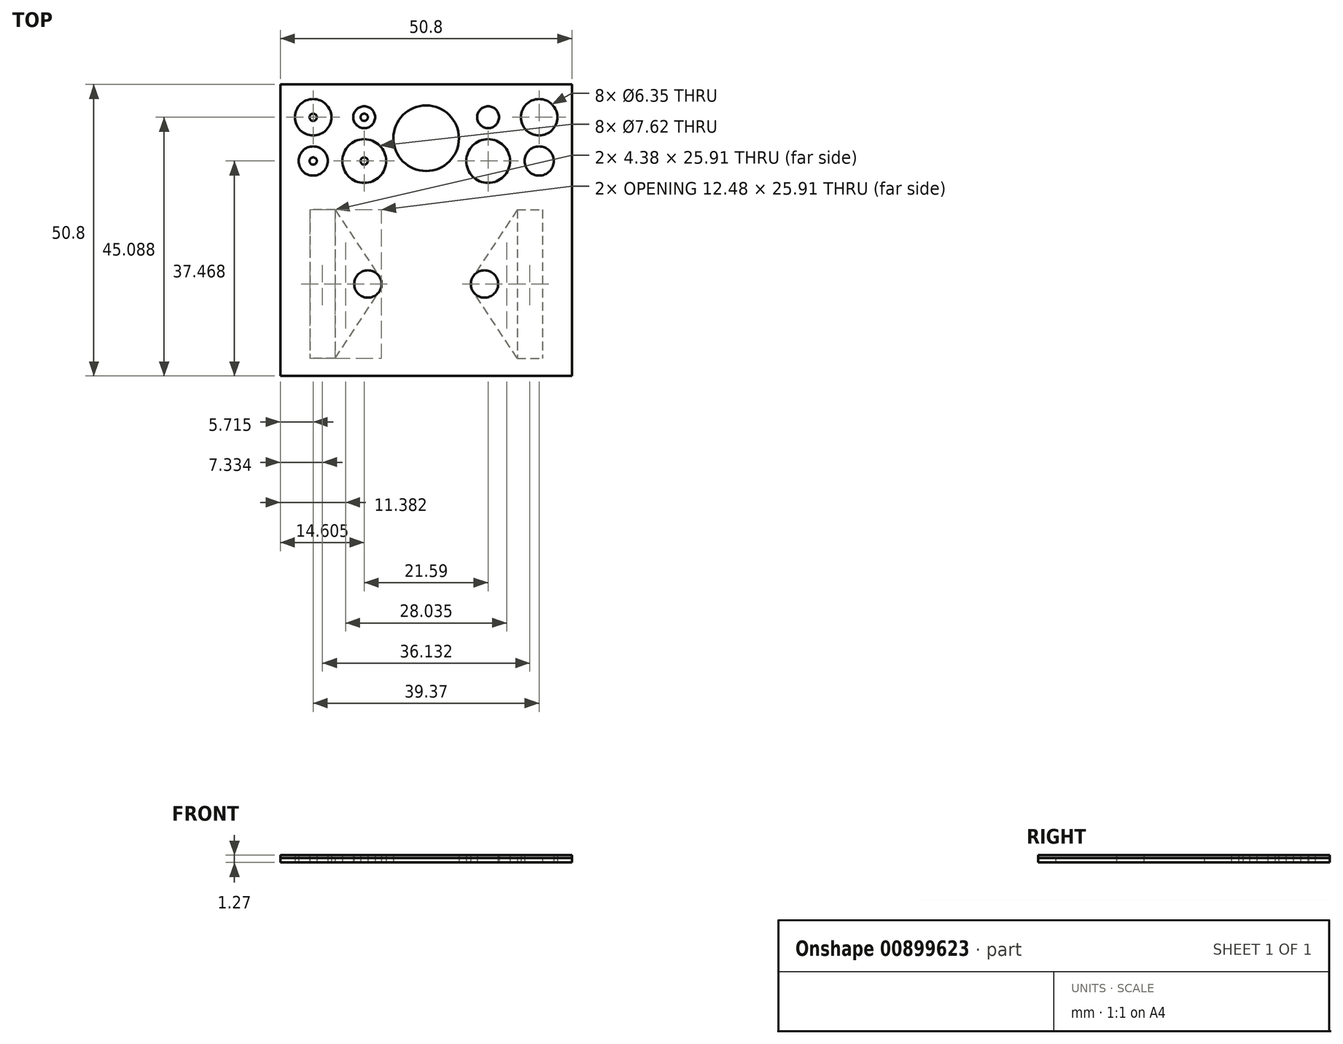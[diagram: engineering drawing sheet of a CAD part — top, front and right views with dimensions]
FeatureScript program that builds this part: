
annotation { "Feature Type Name" : "Feature", "Feature Type Description" : "" }
export const myFeature = defineFeature(function(context is Context, id is Id, definition is map)
    precondition{}
    {
        {
            var Q0;
            Q0=qCreatedBy(makeId("Top.planeOp"),FACE);
            var sketch = newSketch(context, id + "F0", { "sketchPlane" : qUnion([Q0])});
            skLineSegment(sketch, "E0.bottom", {"start": v(25.4, 34.77) * mm, "end": v(-25.4, 34.77) * mm});
            skLineSegment(sketch, "E0.top", {"start": v(25.4, -16.03) * mm, "end": v(-25.4, -16.03) * mm});
            skLineSegment(sketch, "E0.left", {"start": v(25.4, 34.77) * mm, "end": v(25.4, -16.03) * mm});
            skLineSegment(sketch, "E0.right", {"start": v(-25.4, 34.77) * mm, "end": v(-25.4, -16.03) * mm});
            skLineSegment(sketch, "E1", {"start": v(15.88, 12.95) * mm, "end": v(8.17, 1.31) * mm});
            skLineSegment(sketch, "E2", {"start": v(15.88, -12.95) * mm, "end": v(8.17, -1.31) * mm});
            skLineSegment(sketch, "E3.bottom", {"start": v(15.88, 12.95) * mm, "end": v(20.26, 12.95) * mm});
            skLineSegment(sketch, "E3.top", {"start": v(15.88, -12.95) * mm, "end": v(20.26, -12.95) * mm});
            skLineSegment(sketch, "E3.right", {"start": v(20.26, 12.95) * mm, "end": v(20.26, -12.95) * mm});
            skLineSegment(sketch, "E4.MirrorCS", {"start": v(-20.26, 12.95) * mm, "end": v(-20.26, -12.95) * mm});
            skLineSegment(sketch, "E5.MirrorCS", {"start": v(-15.88, 12.95) * mm, "end": v(-20.26, 12.95) * mm});
            skLineSegment(sketch, "E6.MirrorCS", {"start": v(-15.88, 12.95) * mm, "end": v(-8.17, 1.31) * mm});
            skLineSegment(sketch, "E7.MirrorCS", {"start": v(-15.88, -12.95) * mm, "end": v(-8.17, -1.31) * mm});
            skLineSegment(sketch, "E8.MirrorCS", {"start": v(-15.88, -12.95) * mm, "end": v(-20.26, -12.95) * mm});
            skLineSegment(sketch, "E9", {"start": v(0, -16.03) * mm, "end": v(0, 0) * mm, "construction": true});
            skLineSegment(sketch, "E10", {"start": v(0, 0) * mm, "end": v(20.26, 0) * mm, "construction": true});
            skLineSegment(sketch, "E11", {"start": v(-25.4, 16.03) * mm, "end": v(25.4, 16.03) * mm, "construction": true});
            skLineSegment(sketch, "E12", {"start": v(0, 16.03) * mm, "end": v(0, 34.77) * mm, "construction": true});
            skLineSegment(sketch, "E13", {"start": v(10.8, 21.44) * mm, "end": v(19.69, 21.44) * mm, "construction": true});
            skLineSegment(sketch, "E14", {"start": v(19.69, 21.44) * mm, "end": v(19.69, 29.06) * mm, "construction": true});
            skLineSegment(sketch, "E15", {"start": v(19.69, 29.06) * mm, "end": v(10.8, 29.06) * mm, "construction": true});
            skLineSegment(sketch, "E16", {"start": v(10.8, 29.06) * mm, "end": v(10.8, 21.44) * mm, "construction": true});
            skCircle(sketch, "E17", {"center": v(0, 25.4) * mm, "radius": 5.72 * mm});
            skCircle(sketch, "E18", {"center": v(10.8, 29.06) * mm, "radius": 1.9 * mm});
            skCircle(sketch, "E19", {"center": v(10.8, 21.44) * mm, "radius": 3.81 * mm});
            skCircle(sketch, "E20", {"center": v(19.69, 29.06) * mm, "radius": 3.18 * mm});
            skCircle(sketch, "E21", {"center": v(19.69, 21.44) * mm, "radius": 2.54 * mm});
            skCircle(sketch, "E22.MirrorC", {"center": v(-10.8, 29.06) * mm, "radius": 1.9 * mm});
            skCircle(sketch, "E23.MirrorC", {"center": v(-10.8, 21.44) * mm, "radius": 3.81 * mm});
            skCircle(sketch, "E24.MirrorC", {"center": v(-19.69, 29.06) * mm, "radius": 3.18 * mm});
            skCircle(sketch, "E25.MirrorC", {"center": v(-19.69, 21.44) * mm, "radius": 2.54 * mm});
            skLineSegment(sketch, "E26", {"start": v(-15.88, 12.95) * mm, "end": v(-15.88, -12.95) * mm});
            skLineSegment(sketch, "E27", {"start": v(15.88, 12.95) * mm, "end": v(15.88, -12.95) * mm});
            skCircle(sketch, "E28", {"center": v(-10.16, 0) * mm, "radius": 2.38 * mm});
            skCircle(sketch, "E29", {"center": v(10.16, 0) * mm, "radius": 2.38 * mm});
            skCircle(sketch, "E30", {"center": v(-19.69, 29.06) * mm, "radius": 0.64 * mm});
            skCircle(sketch, "E31", {"center": v(-10.8, 29.06) * mm, "radius": 0.64 * mm});
            skCircle(sketch, "E32", {"center": v(-10.8, 21.44) * mm, "radius": 0.64 * mm});
            skCircle(sketch, "E33", {"center": v(-19.69, 21.44) * mm, "radius": 0.64 * mm});
            skSolve(sketch);
        }
        {
            var Q0;
            Q0 = qSketchRegion(id + "F0", true);
            extrude(context, id + "F1", {"entities" : qUnion([Q0]), "depth" : 0.76 * mm, "offsetDistance" : 25.4 * mm});
        }
        {
            var Q0;
            Q0 = qSketchRegion(id + "F0", true);
            var Q1;
            Q1=makeQuery(id+"F0.imprint","IMPRINT",FACE,{"disambiguationData":[TD([[makeQuery(id+"F0.imprint","IMPRINT",EDGE,{"derivedFrom":sQuery(id+"F0.wireOp",EDGE,"E4.MirrorCS")}),1.0]])]});
            var Q2;
            {var subQ0=sQuery(id+"F0.wireOp",EDGE,"E6.MirrorCS");Q2=makeQuery(id+"F0.imprint","IMPRINT",FACE,{"disambiguationData":[TD([[makeQuery(id+"F0.imprint","IMPRINT",EDGE,{"derivedFrom":subQ0}),-1.0]])]});}
            var Q3;
            {var subQ0=sQuery(id+"F0.wireOp",EDGE,"E28");var subQ1=makeQuery(id+"F0.imprint","INTERSECT",VERTEX,{"derivedFrom":[sQuery(id+"F0.wireOp",EDGE,"E6.MirrorCS"),subQ0]});Q3=makeQuery(id+"F0.imprint","IMPRINT",FACE,{"disambiguationData":[TD([[makeQuery(id+"F0.imprint","IMPRINT",EDGE,{"disambiguationData":[TD([[subQ1,-1.0]])],"derivedFrom":subQ0}),1.0]])]});}
            var Q4;
            Q4=makeQuery(id+"F0.imprint","IMPRINT",FACE,{"disambiguationData":[TD([[makeQuery(id+"F0.imprint","IMPRINT",EDGE,{"derivedFrom":sQuery(id+"F0.wireOp",EDGE,"E3.bottom")}),-1.0]])]});
            var Q5;
            {var subQ0=sQuery(id+"F0.wireOp",EDGE,"E1");Q5=makeQuery(id+"F0.imprint","IMPRINT",FACE,{"disambiguationData":[TD([[makeQuery(id+"F0.imprint","IMPRINT",EDGE,{"derivedFrom":subQ0}),1.0]])]});}
            var Q6;
            {var subQ0=sQuery(id+"F0.wireOp",EDGE,"E29");var subQ1=makeQuery(id+"F0.imprint","INTERSECT",VERTEX,{"derivedFrom":[sQuery(id+"F0.wireOp",EDGE,"E1"),subQ0]});Q6=makeQuery(id+"F0.imprint","IMPRINT",FACE,{"disambiguationData":[TD([[makeQuery(id+"F0.imprint","IMPRINT",EDGE,{"disambiguationData":[TD([[subQ1,-1.0]])],"derivedFrom":subQ0}),1.0]])]});}
            var Q7;
            Q7=makeQuery(id+"F0.imprint","IMPRINT",FACE,{"disambiguationData":[TD([[makeQuery(id+"F0.imprint","IMPRINT",EDGE,{"derivedFrom":sQuery(id+"F0.wireOp",EDGE,"E25.MirrorC")}),-1.0]])]});
            var Q8;
            Q8=makeQuery(id+"F0.imprint","IMPRINT",FACE,{"disambiguationData":[TD([[makeQuery(id+"F0.imprint","IMPRINT",EDGE,{"derivedFrom":sQuery(id+"F0.wireOp",EDGE,"E24.MirrorC")}),-1.0]])]});
            var Q9;
            Q9=makeQuery(id+"F0.imprint","IMPRINT",FACE,{"disambiguationData":[TD([[makeQuery(id+"F0.imprint","IMPRINT",EDGE,{"derivedFrom":sQuery(id+"F0.wireOp",EDGE,"E22.MirrorC")}),-1.0]])]});
            var Q10;
            Q10=makeQuery(id+"F0.imprint","IMPRINT",FACE,{"disambiguationData":[TD([[makeQuery(id+"F0.imprint","IMPRINT",EDGE,{"derivedFrom":sQuery(id+"F0.wireOp",EDGE,"E23.MirrorC")}),-1.0]])]});
            var Q11;
            Q11=makeQuery(id+"F0.imprint","IMPRINT",FACE,{"disambiguationData":[TD([[makeQuery(id+"F0.imprint","IMPRINT",EDGE,{"derivedFrom":sQuery(id+"F0.wireOp",EDGE,"E33")}),1.0]])]});
            var Q12;
            Q12=makeQuery(id+"F0.imprint","IMPRINT",FACE,{"disambiguationData":[TD([[makeQuery(id+"F0.imprint","IMPRINT",EDGE,{"derivedFrom":sQuery(id+"F0.wireOp",EDGE,"E32")}),1.0]])]});
            var Q13;
            Q13=makeQuery(id+"F0.imprint","IMPRINT",FACE,{"disambiguationData":[TD([[makeQuery(id+"F0.imprint","IMPRINT",EDGE,{"derivedFrom":sQuery(id+"F0.wireOp",EDGE,"E31")}),1.0]])]});
            var Q14;
            Q14=makeQuery(id+"F0.imprint","IMPRINT",FACE,{"disambiguationData":[TD([[makeQuery(id+"F0.imprint","IMPRINT",EDGE,{"derivedFrom":sQuery(id+"F0.wireOp",EDGE,"E30")}),1.0]])]});
            extrude(context, id + "F2", {"entities" : qUnion([Q0, Q1, Q2, Q3, Q4, Q5, Q6, Q7, Q8, Q9, Q10, Q11, Q12, Q13, Q14]), "depth" : 1.27 * mm, "offsetDistance" : 25.4 * mm});
        }
        {
            var Q0;
            Q0 = qSketchRegion(id + "F0", true);
            var Q1;
            {var subQ0=sQuery(id+"F0.wireOp",EDGE,"E28");var subQ1=makeQuery(id+"F0.imprint","INTERSECT",VERTEX,{"derivedFrom":[sQuery(id+"F0.wireOp",EDGE,"E6.MirrorCS"),subQ0]});Q1=makeQuery(id+"F0.imprint","IMPRINT",FACE,{"disambiguationData":[TD([[makeQuery(id+"F0.imprint","IMPRINT",EDGE,{"disambiguationData":[TD([[subQ1,-1.0]])],"derivedFrom":subQ0}),1.0]])]});}
            var Q2;
            {var subQ0=sQuery(id+"F0.wireOp",EDGE,"E6.MirrorCS");Q2=makeQuery(id+"F0.imprint","IMPRINT",FACE,{"disambiguationData":[TD([[makeQuery(id+"F0.imprint","IMPRINT",EDGE,{"derivedFrom":subQ0}),-1.0]])]});}
            var Q3;
            {var subQ0=sQuery(id+"F0.wireOp",EDGE,"E29");var subQ1=makeQuery(id+"F0.imprint","INTERSECT",VERTEX,{"derivedFrom":[sQuery(id+"F0.wireOp",EDGE,"E1"),subQ0]});Q3=makeQuery(id+"F0.imprint","IMPRINT",FACE,{"disambiguationData":[TD([[makeQuery(id+"F0.imprint","IMPRINT",EDGE,{"disambiguationData":[TD([[subQ1,-1.0]])],"derivedFrom":subQ0}),1.0]])]});}
            var Q4;
            {var subQ0=sQuery(id+"F0.wireOp",EDGE,"E1");Q4=makeQuery(id+"F0.imprint","IMPRINT",FACE,{"disambiguationData":[TD([[makeQuery(id+"F0.imprint","IMPRINT",EDGE,{"derivedFrom":subQ0}),1.0]])]});}
            extrude(context, id + "F3", {"entities" : qUnion([Q0, Q1, Q2, Q3, Q4]), "depth" : 0.76 * mm, "offsetDistance" : 25.4 * mm});
        }
        {
            var Q0;
            Q0 = qSketchRegion(id + "F0", true);
            var Q1;
            Q1=makeQuery(id+"F0.imprint","IMPRINT",FACE,{"disambiguationData":[TD([[makeQuery(id+"F0.imprint","IMPRINT",EDGE,{"derivedFrom":sQuery(id+"F0.wireOp",EDGE,"E4.MirrorCS")}),1.0]])]});
            var Q2;
            Q2=makeQuery(id+"F0.imprint","IMPRINT",FACE,{"disambiguationData":[TD([[makeQuery(id+"F0.imprint","IMPRINT",EDGE,{"derivedFrom":sQuery(id+"F0.wireOp",EDGE,"E3.bottom")}),-1.0]])]});
            var Q3;
            {var subQ0=sQuery(id+"F0.wireOp",EDGE,"E6.MirrorCS");Q3=makeQuery(id+"F0.imprint","IMPRINT",FACE,{"disambiguationData":[TD([[makeQuery(id+"F0.imprint","IMPRINT",EDGE,{"derivedFrom":subQ0}),-1.0]])]});}
            var Q4;
            {var subQ0=sQuery(id+"F0.wireOp",EDGE,"E1");Q4=makeQuery(id+"F0.imprint","IMPRINT",FACE,{"disambiguationData":[TD([[makeQuery(id+"F0.imprint","IMPRINT",EDGE,{"derivedFrom":subQ0}),1.0]])]});}
            var Q5;
            Q5=makeQuery(id+"F0.imprint","IMPRINT",FACE,{"disambiguationData":[TD([[makeQuery(id+"F0.imprint","IMPRINT",EDGE,{"derivedFrom":sQuery(id+"F0.wireOp",EDGE,"E25.MirrorC")}),-1.0]])]});
            var Q6;
            Q6=makeQuery(id+"F0.imprint","IMPRINT",FACE,{"disambiguationData":[TD([[makeQuery(id+"F0.imprint","IMPRINT",EDGE,{"derivedFrom":sQuery(id+"F0.wireOp",EDGE,"E24.MirrorC")}),-1.0]])]});
            var Q7;
            Q7=makeQuery(id+"F0.imprint","IMPRINT",FACE,{"disambiguationData":[TD([[makeQuery(id+"F0.imprint","IMPRINT",EDGE,{"derivedFrom":sQuery(id+"F0.wireOp",EDGE,"E23.MirrorC")}),-1.0]])]});
            var Q8;
            Q8=makeQuery(id+"F0.imprint","IMPRINT",FACE,{"disambiguationData":[TD([[makeQuery(id+"F0.imprint","IMPRINT",EDGE,{"derivedFrom":sQuery(id+"F0.wireOp",EDGE,"E22.MirrorC")}),-1.0]])]});
            extrude(context, id + "F4", {"entities" : qUnion([Q0, Q1, Q2, Q3, Q4, Q5, Q6, Q7, Q8]), "depth" : 1.27 * mm, "offsetDistance" : 25.4 * mm});
        }
        {
            var Q0;
            Q0=makeQuery(id+"F0.imprint","IMPRINT",FACE,{"disambiguationData":[TD([[makeQuery(id+"F0.imprint","IMPRINT",EDGE,{"derivedFrom":sQuery(id+"F0.wireOp",EDGE,"E4.MirrorCS")}),1.0]])]});
            var Q1;
            {var subQ0=sQuery(id+"F0.wireOp",EDGE,"E1");Q1=makeQuery(id+"F0.imprint","IMPRINT",FACE,{"disambiguationData":[TD([[makeQuery(id+"F0.imprint","IMPRINT",EDGE,{"derivedFrom":subQ0}),1.0]])]});}
            var Q2;
            {var subQ0=sQuery(id+"F0.wireOp",EDGE,"E29");var subQ1=makeQuery(id+"F0.imprint","INTERSECT",VERTEX,{"derivedFrom":[sQuery(id+"F0.wireOp",EDGE,"E1"),subQ0]});Q2=makeQuery(id+"F0.imprint","IMPRINT",FACE,{"disambiguationData":[TD([[makeQuery(id+"F0.imprint","IMPRINT",EDGE,{"disambiguationData":[TD([[subQ1,-1.0]])],"derivedFrom":subQ0}),1.0]])]});}
            var Q3;
            Q3=makeQuery(id+"F0.imprint","IMPRINT",FACE,{"disambiguationData":[TD([[makeQuery(id+"F0.imprint","IMPRINT",EDGE,{"derivedFrom":sQuery(id+"F0.wireOp",EDGE,"E17")}),1.0]])]});
            var Q4;
            Q4=makeQuery(id+"F0.imprint","IMPRINT",FACE,{"disambiguationData":[TD([[makeQuery(id+"F0.imprint","IMPRINT",EDGE,{"derivedFrom":sQuery(id+"F0.wireOp",EDGE,"E19")}),1.0]])]});
            var Q5;
            Q5=makeQuery(id+"F0.imprint","IMPRINT",FACE,{"disambiguationData":[TD([[makeQuery(id+"F0.imprint","IMPRINT",EDGE,{"derivedFrom":sQuery(id+"F0.wireOp",EDGE,"E18")}),1.0]])]});
            var Q6;
            Q6=makeQuery(id+"F0.imprint","IMPRINT",FACE,{"disambiguationData":[TD([[makeQuery(id+"F0.imprint","IMPRINT",EDGE,{"derivedFrom":sQuery(id+"F0.wireOp",EDGE,"E20")}),1.0]])]});
            var Q7;
            Q7=makeQuery(id+"F0.imprint","IMPRINT",FACE,{"disambiguationData":[TD([[makeQuery(id+"F0.imprint","IMPRINT",EDGE,{"derivedFrom":sQuery(id+"F0.wireOp",EDGE,"E21")}),1.0]])]});
            extrude(context, id + "F5", {"entities" : qUnion([Q0, Q1, Q2, Q3, Q4, Q5, Q6, Q7]), "depth" : 0.76 * mm, "offsetDistance" : 25.4 * mm});
        }
    });
